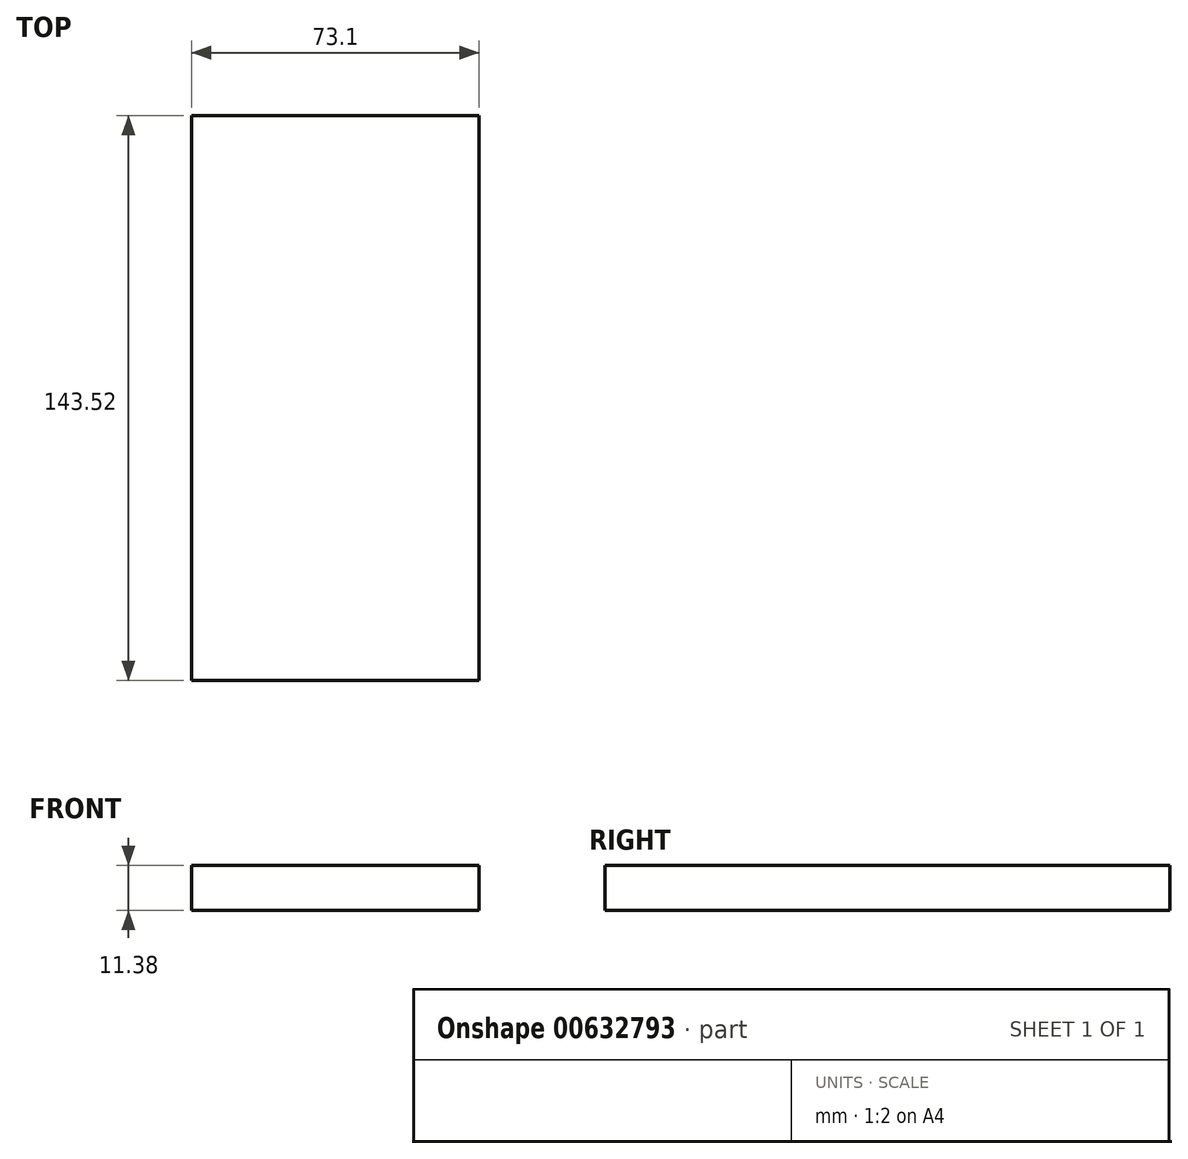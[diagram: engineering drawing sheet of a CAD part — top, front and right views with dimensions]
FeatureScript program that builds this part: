
annotation { "Feature Type Name" : "Feature", "Feature Type Description" : "" }
export const myFeature = defineFeature(function(context is Context, id is Id, definition is map)
    precondition{}
    {
        {
            var Q0;
            Q0=qCreatedBy(makeId("Top.planeOp"),FACE);
            var sketch = newSketch(context, id + "F0", { "sketchPlane" : qUnion([Q0])});
            skLineSegment(sketch, "E0.bottom", {"start": v(0, 0) * mm, "end": v(73.1, 0) * mm});
            skLineSegment(sketch, "E0.top", {"start": v(0, -143.52) * mm, "end": v(73.1, -143.52) * mm});
            skLineSegment(sketch, "E0.left", {"start": v(0, 0) * mm, "end": v(0, -143.52) * mm});
            skLineSegment(sketch, "E0.right", {"start": v(73.1, 0) * mm, "end": v(73.1, -143.52) * mm});
            skSolve(sketch);
        }
        {
            var Q0;
            Q0 = qSketchRegion(id + "F0", true);
            extrude(context, id + "F1", {"entities" : qUnion([Q0]), "depth" : 11.38 * mm, "offsetDistance" : 25 * mm});
        }
    });
